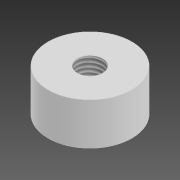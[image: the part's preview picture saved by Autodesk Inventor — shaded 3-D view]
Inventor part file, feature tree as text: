
AUTODESK INVENTOR PART (.ipt)
format: ipt  version: 2020 (Build 240168000, 168)  size: 83,456 bytes
history: native  units: in
note: dims shown in document units (in); Inventor stores cm internally (conversion verified against a paired STEP export)
features: extrude x1, thread x1, sketch x1
ambient origin geometry x8: Origin, YZ Plane, XZ Plane, XY Plane, X Axis, Y Axis, Z Axis, Center Point
bodies: Solid1 (feature_tree)
feature tree (3):
  extrude  "Extrusion1"  Depth=0.1969in
  thread  "Thread1"  [1 undecoded]
  sketch  "Sketch1"  dims[d0=0.3937in d1=0.1181in d2=0.1969in d3=0.0in d4=0.5512in d5=0.0in]
note: 1 required parameter value undecoded (feature->parameter linkage not recoverable at this tier; creation-order binding heuristic only, values carry confidence <= 0.55)
